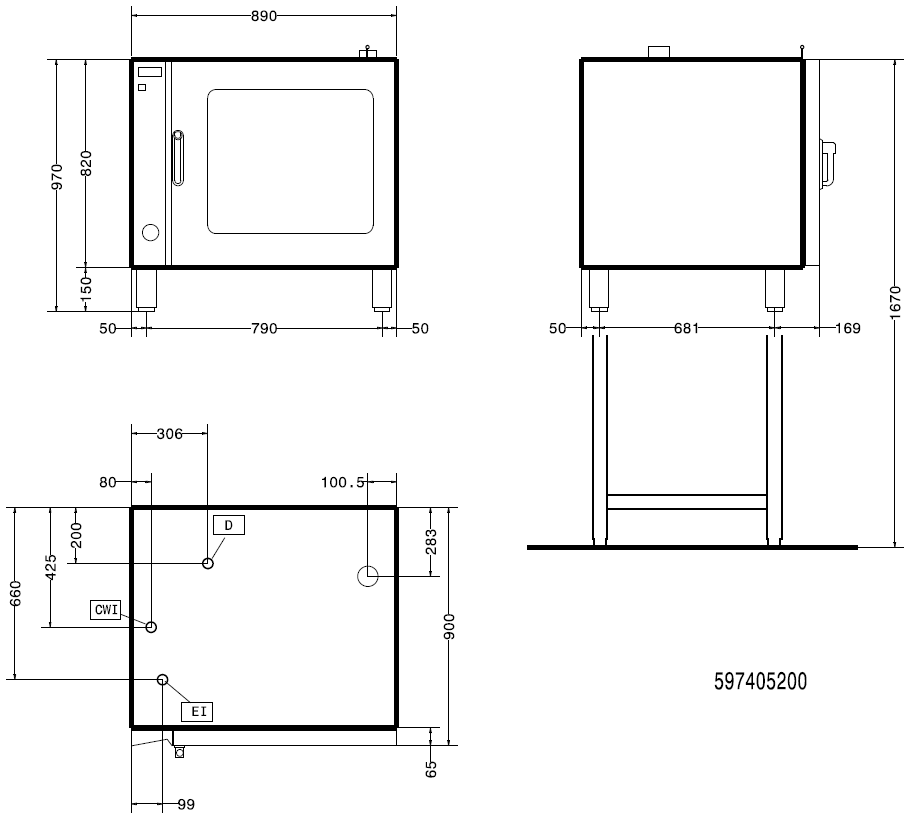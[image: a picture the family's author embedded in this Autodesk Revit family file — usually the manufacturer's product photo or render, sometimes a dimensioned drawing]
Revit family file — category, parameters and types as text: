
# Revit family: QF_ELECTROLUXPROFESSIONAL_240003_FCF6EOEM
name_source: partatom
category: Specialty Equipment
revit_build: Autodesk Revit 2018 (Build: 20190510_1515(x64)
units: mm (PartAtom-declared; Revit-internal decimal feet)

## family parameters
Always vertical = Yes
Cut with Voids When Loaded = No
Part Type = Normal
Room Calculation Point = No
Round Connector Dimension = Use Diameter
Shared = No
Work Plane-Based = No

## types (1)
- Standard
    Accessory = Yes
    Cold Water Size = 19 mm
    Compressed Air Pressure = 0.0 Pa
    Compressed Air Size = 0 mm
    Compressed Air Volume = 0.0 L/s
    Condensate Return Size = 0 mm
    Cycle = 50 Hz
    Depth Actual = 746 mm  [stored 2.44751 ft]
    Description = EL.CONV.OVEN 6GN1/1-SMART STEAM
    Direct Waste Size = 25 mm
    Gas Input Pressure = 0
    Gas KW = 0
    Gas Size = 0 mm
    HP = 10.3 HP
    Height Actual = 633 mm  [stored 2.07677 ft]
    Hot Water Size = 0 mm
    Item Number = 240003
    Length Actual = 860 mm
    Manufacturer = Electrolux Professional
    Model = FCF6EOEM
    Phase = 3
    Refrigerant Compressor Remote = Yes
    Refrigeration Liquid Line Size = 0 mm
    Refrigeration Suction Line Size = 0 mm
    Steam Pounds per Hour = 0
    Steam Supply Maximum Pressure = 0.0 Pa
    Steam Supply Minimum Pressure = 0.0 Pa
    Steam Supply Size = 0 mm
    URL = http://professional.electrolux.com
    URL Manufacturer = http://professional.electrolux.com
    Volts = 380 V
    Watts = 0 W
    Weight = 79.50 kg

note: source unit labels omitted for Gas Input Pressure — the stored unit's dimension contradicts the parameter name (converter mislabeling)

note: [stored X ft] marks values corroborated as IEEE doubles in the binary element streams (Revit-internal decimal feet)

## geometry (parser evidence)
native form markers: Sweep x3
no freeform markers — native parametric forms only
